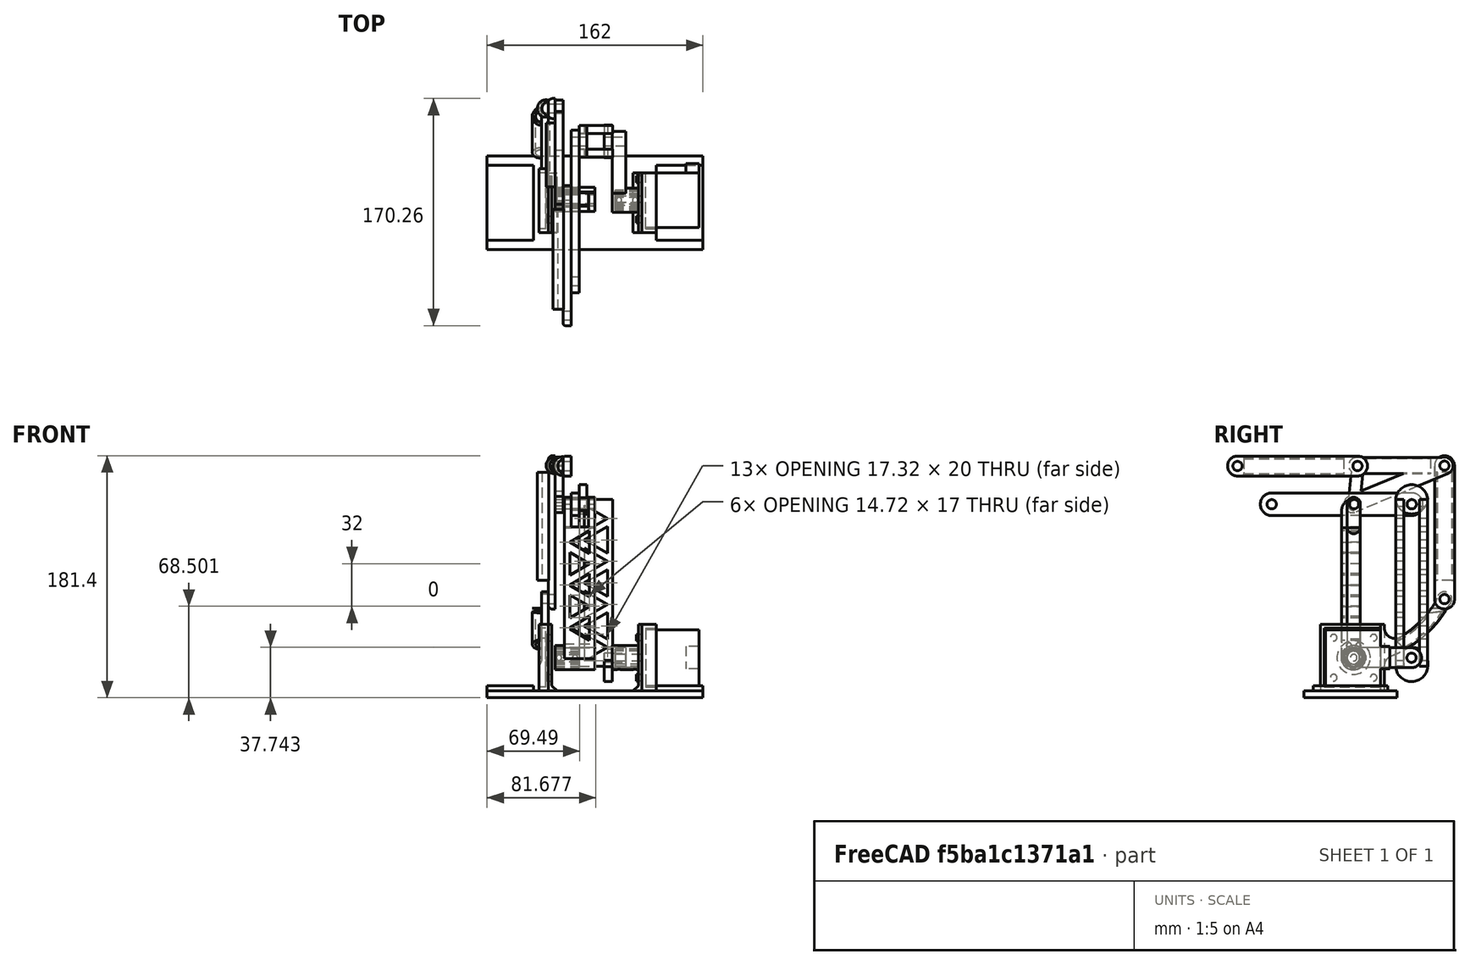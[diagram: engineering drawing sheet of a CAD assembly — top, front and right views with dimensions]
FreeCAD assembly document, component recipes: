
FREECAD ASSEMBLY — COMPONENT RECIPES ("my_arm2")

This assembly document has 21 components, labeled P0..P20 below (a component is one placed body or linked part). 0 of them carry a construction recipe — the FreeCAD feature program that regenerates the part from scratch, quoted from this document or its linked companion documents; the rest are supplied as boundary geometry only. No exploded tour is included for this assembly.
COMPONENT P0 — geometry summary ("union base motor001"; no construction recipe available for this part):
  bounding box: 50.0 x 45.0 x 2.5 mm
  tessellated surface: 2,552 triangles
  volume: 4201 mm^3 (75% of its bounding box)
  symmetry: mirror-symmetric across its z mid-plane
COMPONENT P1 — geometry summary ("tonillo motor005"; no construction recipe available for this part):
  bounding box: 5.0 x 5.0 x 4.0 mm
  tessellated surface: 500 triangles
  volume: 79 mm^3 (79% of its bounding box)
  symmetry: 2-fold rotationally symmetric about the x axis; 2-fold rotationally symmetric about the y axis; revolution-symmetric about the z axis through its bounding-box center; mirror-symmetric across its x mid-plane, y mid-plane
COMPONENT P2 — geometry summary ("tonillo motor006"; no construction recipe available for this part):
  bounding box: 5.0 x 5.0 x 4.0 mm
  tessellated surface: 500 triangles
  volume: 79 mm^3 (79% of its bounding box)
  symmetry: 2-fold rotationally symmetric about the x axis; 2-fold rotationally symmetric about the y axis; revolution-symmetric about the z axis through its bounding-box center; mirror-symmetric across its x mid-plane, y mid-plane
COMPONENT P3 — geometry summary ("tonillo motor007"; no construction recipe available for this part):
  bounding box: 5.0 x 5.0 x 4.0 mm
  tessellated surface: 500 triangles
  volume: 79 mm^3 (79% of its bounding box)
  symmetry: 2-fold rotationally symmetric about the x axis; 2-fold rotationally symmetric about the y axis; revolution-symmetric about the z axis through its bounding-box center; mirror-symmetric across its x mid-plane, y mid-plane
COMPONENT P4 — geometry summary ("lateral der"; no construction recipe available for this part):
  bounding box: 45.0 x 8.0 x 3.0 mm
  tessellated surface: 12 triangles
  volume: 1080 mm^3 (100% of its bounding box)
  symmetry: 2-fold rotationally symmetric about the y axis; 2-fold rotationally symmetric about the z axis; mirror-symmetric across its y mid-plane
COMPONENT P5 — geometry summary ("tonillo motor008"; no construction recipe available for this part):
  bounding box: 5.0 x 5.0 x 4.0 mm
  tessellated surface: 500 triangles
  volume: 79 mm^3 (79% of its bounding box)
  symmetry: 2-fold rotationally symmetric about the x axis; 2-fold rotationally symmetric about the y axis; revolution-symmetric about the z axis through its bounding-box center; mirror-symmetric across its x mid-plane, y mid-plane
COMPONENT P6 — geometry summary ("lateral der001"; no construction recipe available for this part):
  bounding box: 45.0 x 8.0 x 3.0 mm
  tessellated surface: 12 triangles
  volume: 1080 mm^3 (100% of its bounding box)
  symmetry: 2-fold rotationally symmetric about the y axis; 2-fold rotationally symmetric about the z axis; mirror-symmetric across its y mid-plane
COMPONENT P7 — geometry summary ("tonillo motor010"; no construction recipe available for this part):
  bounding box: 5.0 x 5.0 x 4.0 mm
  tessellated surface: 500 triangles
  volume: 79 mm^3 (79% of its bounding box)
  symmetry: 2-fold rotationally symmetric about the x axis; 2-fold rotationally symmetric about the y axis; revolution-symmetric about the z axis through its bounding-box center; mirror-symmetric across its x mid-plane, y mid-plane
COMPONENT P8 — geometry summary ("tonillo motor011"; no construction recipe available for this part):
  bounding box: 5.0 x 5.0 x 4.0 mm
  tessellated surface: 500 triangles
  volume: 79 mm^3 (79% of its bounding box)
  symmetry: 2-fold rotationally symmetric about the x axis; 2-fold rotationally symmetric about the y axis; revolution-symmetric about the z axis through its bounding-box center; mirror-symmetric across its x mid-plane, y mid-plane
COMPONENT P9 — geometry summary ("soporte motor001"; no construction recipe available for this part):
  bounding box: 56.0 x 35.0 x 4.0 mm
  tessellated surface: 12 triangles
  volume: 7840 mm^3 (100% of its bounding box)
  symmetry: 2-fold rotationally symmetric about the x axis; 2-fold rotationally symmetric about the y axis; 2-fold rotationally symmetric about the z axis; mirror-symmetric across its x mid-plane, y mid-plane, z mid-plane
COMPONENT P10 — geometry summary ("tonillo motor012"; no construction recipe available for this part):
  bounding box: 8.0 x 5.0 x 5.0 mm
  tessellated surface: 500 triangles
  volume: 157 mm^3 (79% of its bounding box)
  symmetry: 2-fold rotationally symmetric about the y axis; 6-fold rotationally symmetric about the z axis; mirror-symmetric across its y mid-plane, z mid-plane
COMPONENT P11 — geometry summary ("lateral der002"; no construction recipe available for this part):
  bounding box: 45.0 x 8.0 x 3.0 mm
  tessellated surface: 12 triangles
  volume: 1080 mm^3 (100% of its bounding box)
  symmetry: 2-fold rotationally symmetric about the y axis; 2-fold rotationally symmetric about the z axis; mirror-symmetric across its y mid-plane
COMPONENT P12 — geometry summary ("tonillo motor014"; no construction recipe available for this part):
  bounding box: 8.0 x 5.0 x 5.0 mm
  tessellated surface: 500 triangles
  volume: 157 mm^3 (79% of its bounding box)
  symmetry: 2-fold rotationally symmetric about the y axis; 6-fold rotationally symmetric about the z axis; mirror-symmetric across its y mid-plane, z mid-plane
COMPONENT P13 — geometry summary ("tonillo motor015"; no construction recipe available for this part):
  bounding box: 8.0 x 5.0 x 5.0 mm
  tessellated surface: 500 triangles
  volume: 157 mm^3 (79% of its bounding box)
  symmetry: 2-fold rotationally symmetric about the y axis; 6-fold rotationally symmetric about the z axis; mirror-symmetric across its y mid-plane, z mid-plane
COMPONENT P14 — geometry summary ("Palo triangular001"; no construction recipe available for this part):
  bounding box: 125.0 x 25.0 x 6.0 mm
  tessellated surface: 124 triangles
  volume: 11475 mm^3 (61% of its bounding box)
  symmetry: mirror-symmetric across its y mid-plane, z mid-plane
COMPONENT P15 — geometry summary ("union centro_arriba001"; no construction recipe available for this part):
  bounding box: 27.3 x 10.0 x 5.0 mm
  tessellated surface: 1,016 triangles
  volume: 1066 mm^3 (78% of its bounding box)
COMPONENT P16 — geometry summary ("tonillo motor016"; no construction recipe available for this part):
  bounding box: 8.0 x 5.0 x 5.0 mm
  tessellated surface: 500 triangles
  volume: 157 mm^3 (79% of its bounding box)
  symmetry: 2-fold rotationally symmetric about the y axis; 6-fold rotationally symmetric about the z axis; mirror-symmetric across its y mid-plane, z mid-plane
COMPONENT P17 — geometry summary ("tonillo motor017"; no construction recipe available for this part):
  bounding box: 8.0 x 5.0 x 5.0 mm
  tessellated surface: 500 triangles
  volume: 157 mm^3 (79% of its bounding box)
  symmetry: 2-fold rotationally symmetric about the y axis; 6-fold rotationally symmetric about the z axis; mirror-symmetric across its y mid-plane, z mid-plane
COMPONENT P18 — geometry summary ("tonillo motor018"; no construction recipe available for this part):
  bounding box: 8.0 x 5.0 x 5.0 mm
  tessellated surface: 500 triangles
  volume: 157 mm^3 (79% of its bounding box)
  symmetry: 2-fold rotationally symmetric about the y axis; 6-fold rotationally symmetric about the z axis; mirror-symmetric across its y mid-plane, z mid-plane
COMPONENT P19 — geometry summary ("union centro_arriba003"; no construction recipe available for this part):
  bounding box: 27.3 x 10.0 x 5.0 mm
  tessellated surface: 1,016 triangles
  volume: 1066 mm^3 (78% of its bounding box)
COMPONENT P20 — geometry summary ("Union codo1"; no construction recipe available for this part):
  bounding box: 26.9 x 16.5 x 6.0 mm
  tessellated surface: 1,016 triangles
  volume: 2083 mm^3 (78% of its bounding box)
  symmetry: 2-fold rotationally symmetric about the y axis; mirror-symmetric across its x mid-plane, z mid-plane
PROVENANCE & LICENSES
A FreeCAD (.FCStd) document from a public repository crawl; recipes are the document's own serialized feature recipes (and, for linked parts, companion documents' recipes).
License: lgpl-2.1.
